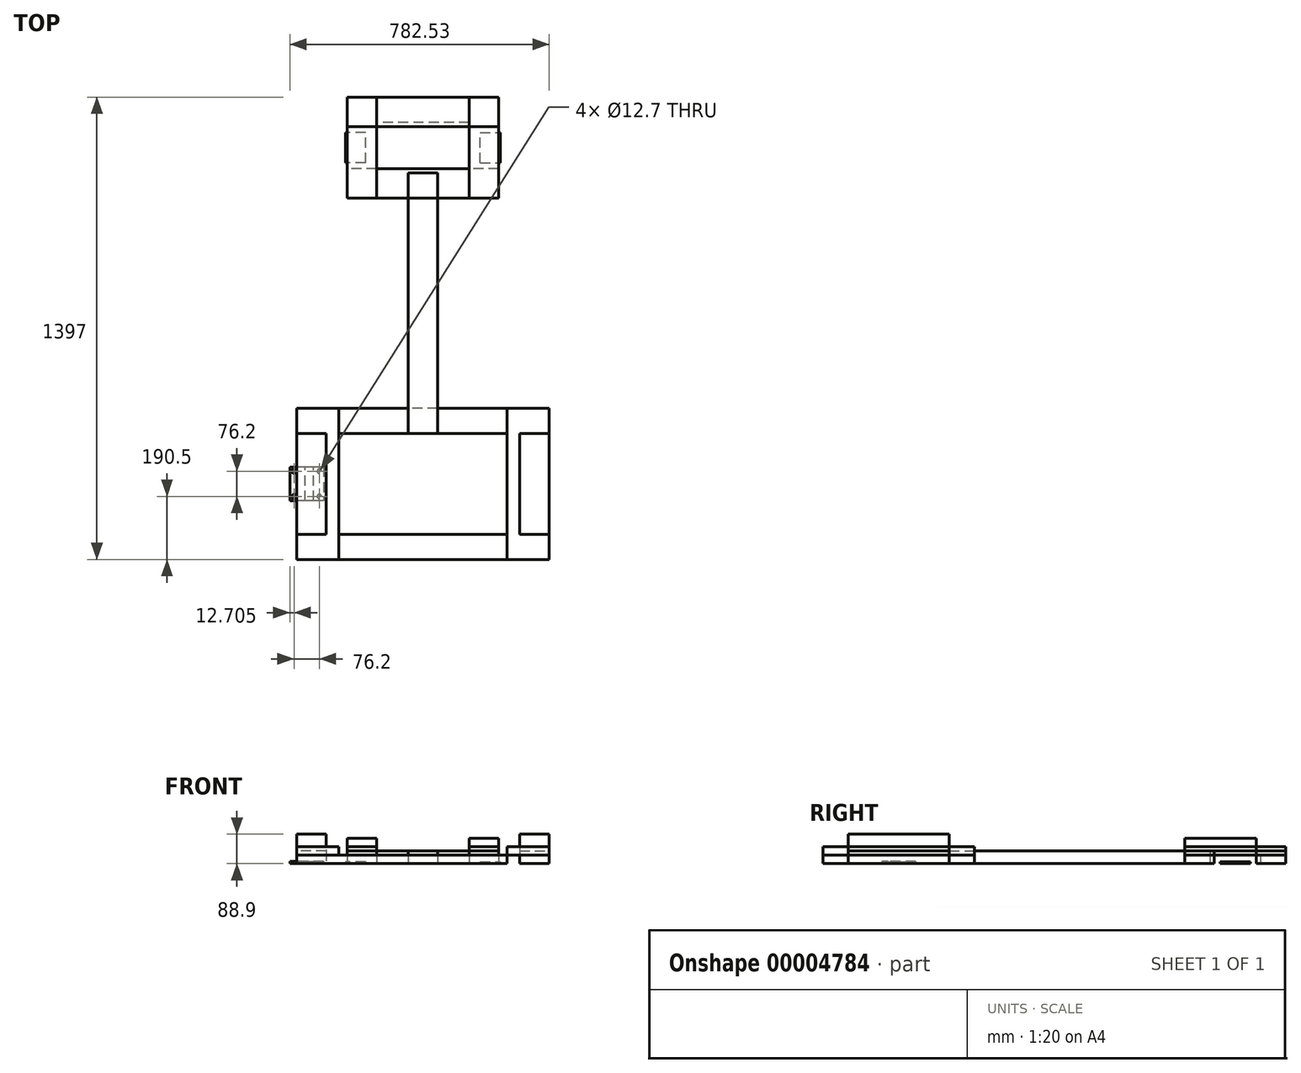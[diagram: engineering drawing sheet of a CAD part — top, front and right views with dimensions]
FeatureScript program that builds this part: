
annotation { "Feature Type Name" : "Feature", "Feature Type Description" : "" }
export const myFeature = defineFeature(function(context is Context, id is Id, definition is map)
    precondition{}
    {
        {
            var Q0;
            Q0=qCreatedBy(makeId("Top.planeOp"),FACE);
            var sketch = newSketch(context, id + "F0", { "sketchPlane" : qUnion([Q0])});
            skLineSegment(sketch, "E0.bottom", {"start": v(44.45, 152.4) * mm, "end": v(-44.45, 152.4) * mm});
            skLineSegment(sketch, "E0.top", {"start": v(44.45, 939.8) * mm, "end": v(-44.45, 939.8) * mm});
            skLineSegment(sketch, "E0.left", {"start": v(44.45, 152.4) * mm, "end": v(44.45, 939.8) * mm});
            skLineSegment(sketch, "E0.right", {"start": v(-44.45, 152.4) * mm, "end": v(-44.45, 939.8) * mm});
            skPoint(sketch, "E0.middle", {"position": v(0, 546.1) * mm});
            skLineSegment(sketch, "E1.bottom", {"start": v(-254, -228.6) * mm, "end": v(-381, -228.6) * mm});
            skLineSegment(sketch, "E1.top", {"start": v(-254, 228.6) * mm, "end": v(-381, 228.6) * mm});
            skLineSegment(sketch, "E1.left", {"start": v(-254, -228.6) * mm, "end": v(-254, 228.6) * mm});
            skLineSegment(sketch, "E1.right", {"start": v(-381, -228.6) * mm, "end": v(-381, 228.6) * mm});
            skPoint(sketch, "E1.middle", {"position": v(-317.5, 0) * mm});
            skLineSegment(sketch, "E2.MirrorCS", {"start": v(254, 228.6) * mm, "end": v(381, 228.6) * mm});
            skLineSegment(sketch, "E3.MirrorCS", {"start": v(381, -228.6) * mm, "end": v(381, 228.6) * mm});
            skLineSegment(sketch, "E4.MirrorCS", {"start": v(254, -228.6) * mm, "end": v(254, 228.6) * mm});
            skLineSegment(sketch, "E5.MirrorCS", {"start": v(254, -228.6) * mm, "end": v(381, -228.6) * mm});
            skLineSegment(sketch, "E6.bottom", {"start": v(381, 152.4) * mm, "end": v(-381, 152.4) * mm});
            skLineSegment(sketch, "E6.top", {"start": v(381, 228.6) * mm, "end": v(-381, 228.6) * mm});
            skLineSegment(sketch, "E6.left", {"start": v(381, 152.4) * mm, "end": v(381, 228.6) * mm});
            skLineSegment(sketch, "E6.right", {"start": v(-381, 152.4) * mm, "end": v(-381, 228.6) * mm});
            skPoint(sketch, "E6.middle", {"position": v(0, 190.5) * mm});
            skPoint(sketch, "E7.MirrorP", {"position": v(0, -190.5) * mm});
            skLineSegment(sketch, "E8.MirrorCS", {"start": v(381, -228.6) * mm, "end": v(-381, -228.6) * mm});
            skLineSegment(sketch, "E9.MirrorCS", {"start": v(381, -152.4) * mm, "end": v(381, -228.6) * mm});
            skLineSegment(sketch, "E10.MirrorCS", {"start": v(-381, 228.6) * mm, "end": v(-381, -228.6) * mm});
            skLineSegment(sketch, "E11.MirrorCS", {"start": v(381, -152.4) * mm, "end": v(-381, -152.4) * mm});
            skLineSegment(sketch, "E12.bottom", {"start": v(-139.7, 863.6) * mm, "end": v(-228.6, 863.6) * mm});
            skLineSegment(sketch, "E12.top", {"start": v(-139.7, 1168.4) * mm, "end": v(-228.6, 1168.4) * mm});
            skLineSegment(sketch, "E12.left", {"start": v(-139.7, 863.6) * mm, "end": v(-139.7, 1168.4) * mm});
            skLineSegment(sketch, "E12.right", {"start": v(-228.6, 863.6) * mm, "end": v(-228.6, 1168.4) * mm});
            skPoint(sketch, "E12.middle", {"position": v(-184.15, 1016) * mm});
            skLineSegment(sketch, "E13", {"start": v(0, 0) * mm, "end": v(0, 2577.34) * mm, "construction": true});
            skLineSegment(sketch, "E14.MirrorCS", {"start": v(139.7, 863.6) * mm, "end": v(139.7, 1168.4) * mm});
            skLineSegment(sketch, "E15.MirrorCS", {"start": v(139.7, 863.6) * mm, "end": v(228.6, 863.6) * mm});
            skLineSegment(sketch, "E16.MirrorCS", {"start": v(228.6, 863.6) * mm, "end": v(228.6, 1168.4) * mm});
            skLineSegment(sketch, "E17.MirrorCS", {"start": v(139.7, 1168.4) * mm, "end": v(228.6, 1168.4) * mm});
            skLineSegment(sketch, "E18", {"start": v(-560.55, 1016) * mm, "end": v(837.57, 1016) * mm, "construction": true});
            skPoint(sketch, "E18.startSnap0", {"position": v(-228.6, 1016) * mm});
            skPoint(sketch, "E18.endSnap0", {"position": v(-228.6, 1016) * mm});
            skLineSegment(sketch, "E19.bottom", {"start": v(228.6, 1092.2) * mm, "end": v(-228.6, 1092.2) * mm});
            skLineSegment(sketch, "E19.top", {"start": v(228.6, 1168.4) * mm, "end": v(-228.6, 1168.4) * mm});
            skLineSegment(sketch, "E19.left", {"start": v(228.6, 1092.2) * mm, "end": v(228.6, 1168.4) * mm});
            skLineSegment(sketch, "E19.right", {"start": v(-228.6, 1092.2) * mm, "end": v(-228.6, 1168.4) * mm});
            skPoint(sketch, "E19.middle", {"position": v(0, 1130.3) * mm});
            skLineSegment(sketch, "E20.MirrorCS", {"start": v(228.6, 939.8) * mm, "end": v(-228.6, 939.8) * mm});
            skLineSegment(sketch, "E21.MirrorCS", {"start": v(-228.6, 939.8) * mm, "end": v(-228.6, 863.6) * mm});
            skLineSegment(sketch, "E22.MirrorCS", {"start": v(228.6, 863.6) * mm, "end": v(-228.6, 863.6) * mm});
            skLineSegment(sketch, "E23.MirrorCS", {"start": v(228.6, 939.8) * mm, "end": v(228.6, 863.6) * mm});
            skSolve(sketch);
        }
        {
            var Q0;
            Q0=qCreatedBy(makeId("Top.planeOp"),FACE);
            var sketch = newSketch(context, id + "F1", { "sketchPlane" : qUnion([Q0])});
            skLineSegment(sketch, "E24.bottom", {"start": v(-292.1, -152.4) * mm, "end": v(-381, -152.4) * mm});
            skLineSegment(sketch, "E24.top", {"start": v(-292.1, 152.4) * mm, "end": v(-381, 152.4) * mm});
            skLineSegment(sketch, "E24.left", {"start": v(-292.1, -152.4) * mm, "end": v(-292.1, 152.4) * mm});
            skLineSegment(sketch, "E24.right", {"start": v(-381, -152.4) * mm, "end": v(-381, 152.4) * mm});
            skPoint(sketch, "E24.middle", {"position": v(-336.55, 0) * mm});
            skLineSegment(sketch, "E25.MirrorCS", {"start": v(292.1, 152.4) * mm, "end": v(381, 152.4) * mm});
            skLineSegment(sketch, "E26.MirrorCS", {"start": v(292.1, -152.4) * mm, "end": v(292.1, 152.4) * mm});
            skLineSegment(sketch, "E27.MirrorCS", {"start": v(381, -152.4) * mm, "end": v(381, 152.4) * mm});
            skLineSegment(sketch, "E28.MirrorCS", {"start": v(292.1, -152.4) * mm, "end": v(381, -152.4) * mm});
            skLineSegment(sketch, "E29.bottom", {"start": v(228.6, 1168.4) * mm, "end": v(-228.6, 1168.4) * mm});
            skLineSegment(sketch, "E29.top", {"start": v(228.6, 1079.5) * mm, "end": v(-228.6, 1079.5) * mm});
            skLineSegment(sketch, "E29.left", {"start": v(228.6, 1168.4) * mm, "end": v(228.6, 1079.5) * mm});
            skLineSegment(sketch, "E29.right", {"start": v(-228.6, 1168.4) * mm, "end": v(-228.6, 1079.5) * mm});
            skPoint(sketch, "E29.middle", {"position": v(0, 1123.95) * mm});
            skLineSegment(sketch, "E30.MirrorCS", {"start": v(228.6, 952.5) * mm, "end": v(-228.6, 952.5) * mm});
            skLineSegment(sketch, "E31.MirrorCS", {"start": v(228.6, 863.6) * mm, "end": v(-228.6, 863.6) * mm});
            skLineSegment(sketch, "E32.MirrorCS", {"start": v(228.6, 863.6) * mm, "end": v(228.6, 952.5) * mm});
            skLineSegment(sketch, "E33.MirrorCS", {"start": v(-228.6, 863.6) * mm, "end": v(-228.6, 952.5) * mm});
            skLineSegment(sketch, "E34.bottom", {"start": v(-139.7, 863.6) * mm, "end": v(-228.6, 863.6) * mm});
            skLineSegment(sketch, "E34.top", {"start": v(-139.7, 1168.4) * mm, "end": v(-228.6, 1168.4) * mm});
            skLineSegment(sketch, "E34.left", {"start": v(-139.7, 863.6) * mm, "end": v(-139.7, 1168.4) * mm});
            skLineSegment(sketch, "E34.right", {"start": v(-228.6, 863.6) * mm, "end": v(-228.6, 1168.4) * mm});
            skPoint(sketch, "E34.middle", {"position": v(-184.15, 1016) * mm});
            skLineSegment(sketch, "E35.MirrorCS", {"start": v(139.7, 1168.4) * mm, "end": v(228.6, 1168.4) * mm});
            skLineSegment(sketch, "E36.MirrorCS", {"start": v(228.6, 863.6) * mm, "end": v(228.6, 1168.4) * mm});
            skLineSegment(sketch, "E37.MirrorCS", {"start": v(139.7, 863.6) * mm, "end": v(139.7, 1168.4) * mm});
            skLineSegment(sketch, "E38.MirrorCS", {"start": v(-228.6, 863.6) * mm, "end": v(228.6, 863.6) * mm});
            skLineSegment(sketch, "E39.bottom", {"start": v(-323.85, -228.6) * mm, "end": v(-349.25, -228.6) * mm});
            skLineSegment(sketch, "E39.top", {"start": v(-323.85, 228.6) * mm, "end": v(-349.25, 228.6) * mm});
            skLineSegment(sketch, "E39.left", {"start": v(-323.85, -228.6) * mm, "end": v(-323.85, 228.6) * mm});
            skLineSegment(sketch, "E39.right", {"start": v(-349.25, -228.6) * mm, "end": v(-349.25, 228.6) * mm});
            skSolve(sketch);
        }
        {
            var Q0;
            Q0=makeQuery(id+"F1.imprint","IMPRINT",FACE,{"disambiguationData":[TD([[makeQuery(id+"F1.imprint","IMPRINT",EDGE,{"derivedFrom":sQuery(id+"F1.wireOp",EDGE,"E24.bottom")}),-1.0]])]});
            var Q1;
            Q1=makeQuery(id+"F1.imprint","IMPRINT",FACE,{"disambiguationData":[TD([[makeQuery(id+"F1.imprint","IMPRINT",EDGE,{"derivedFrom":sQuery(id+"F1.wireOp",EDGE,"E25.MirrorCS")}),-1.0]])]});
            extrude(context, id + "F2", {"entities" : qUnion([Q0, Q1]), "depth" : 88.9 * mm, "offsetDistance" : 25.4 * mm});
        }
        {
            var Q0;
            Q0=makeQuery(id+"F1.imprint","IMPRINT",FACE,{"disambiguationData":[TD([[makeQuery(id+"F1.imprint","IMPRINT",EDGE,{"derivedFrom":sQuery(id+"F1.wireOp",EDGE,"E24.bottom")}),-1.0]])]});
            var Q1;
            Q1=makeQuery(id+"F1.imprint","IMPRINT",FACE,{"disambiguationData":[TD([[makeQuery(id+"F1.imprint","IMPRINT",EDGE,{"derivedFrom":sQuery(id+"F1.wireOp",EDGE,"E25.MirrorCS")}),-1.0]])]});
            extrude(context, id + "F3", {"entities" : qUnion([Q0, Q1]), "depth" : 38.1 * mm, "offsetDistance" : 25.4 * mm});
        }
        {
            var Q0;
            {var subQ0=sQuery(id+"F1.wireOp",EDGE,"E37.MirrorCS");var subQ1=sQuery(id+"F1.wireOp",EDGE,"E30.MirrorCS");var subQ2=makeQuery(id+"F1.imprint","INTERSECT",VERTEX,{"derivedFrom":[subQ1,subQ0]});Q0=makeQuery(id+"F1.imprint","IMPRINT",FACE,{"disambiguationData":[TD([[makeQuery(id+"F1.imprint","IMPRINT",EDGE,{"disambiguationData":[TD([[subQ2,-1.0]])],"derivedFrom":subQ1}),1.0]])]});}
            var Q1;
            {var subQ0=sQuery(id+"F1.wireOp",EDGE,"E36.MirrorCS");var subQ1=sQuery(id+"F1.wireOp",EDGE,"E30.MirrorCS");var subQ2=makeQuery(id+"F1.imprint","INTERSECT",VERTEX,{"derivedFrom":[subQ1,subQ0]});Q1=makeQuery(id+"F1.imprint","IMPRINT",FACE,{"disambiguationData":[TD([[makeQuery(id+"F1.imprint","IMPRINT",EDGE,{"disambiguationData":[TD([[subQ2,-1.0]])],"derivedFrom":subQ1}),1.0]])]});}
            var Q2;
            {var subQ0=sQuery(id+"F1.wireOp",EDGE,"E34.right");var subQ1=sQuery(id+"F1.wireOp",EDGE,"E30.MirrorCS");var subQ2=makeQuery(id+"F1.imprint","INTERSECT",VERTEX,{"derivedFrom":[subQ1,subQ0]});Q2=makeQuery(id+"F1.imprint","IMPRINT",FACE,{"disambiguationData":[TD([[makeQuery(id+"F1.imprint","IMPRINT",EDGE,{"disambiguationData":[TD([[subQ2,1.0]])],"derivedFrom":subQ1}),1.0]])]});}
            var Q3;
            {var subQ5=sQuery(id+"F1.wireOp",EDGE,"E34.top");Q3=makeQuery(id+"F1.imprint","IMPRINT",FACE,{"disambiguationData":[TD([[makeQuery(id+"F1.imprint","IMPRINT",EDGE,{"derivedFrom":subQ5}),1.0]])]});}
            var Q4;
            {var subQ0=sQuery(id+"F1.wireOp",EDGE,"E29.bottom");Q4=makeQuery(id+"F1.imprint","IMPRINT",FACE,{"disambiguationData":[TD([[makeQuery(id+"F1.imprint","IMPRINT",EDGE,{"derivedFrom":subQ0}),1.0]])]});}
            var Q5;
            {var subQ5=sQuery(id+"F1.wireOp",EDGE,"E35.MirrorCS");Q5=makeQuery(id+"F1.imprint","IMPRINT",FACE,{"disambiguationData":[TD([[makeQuery(id+"F1.imprint","IMPRINT",EDGE,{"derivedFrom":subQ5}),-1.0]])]});}
            extrude(context, id + "F4", {"entities" : qUnion([Q0, Q1, Q2, Q3, Q4, Q5]), "depth" : 38.1 * mm, "offsetDistance" : 25.4 * mm});
        }
        {
            var Q0;
            {var subQ5=sQuery(id+"F1.wireOp",EDGE,"E34.top");Q0=makeQuery(id+"F1.imprint","IMPRINT",FACE,{"disambiguationData":[TD([[makeQuery(id+"F1.imprint","IMPRINT",EDGE,{"derivedFrom":subQ5}),1.0]])]});}
            var Q1;
            {var subQ0=sQuery(id+"F1.wireOp",EDGE,"E34.right");var subQ1=sQuery(id+"F1.wireOp",EDGE,"E29.top");var subQ2=makeQuery(id+"F1.imprint","INTERSECT",VERTEX,{"derivedFrom":[subQ1,subQ0]});Q1=makeQuery(id+"F1.imprint","IMPRINT",FACE,{"disambiguationData":[TD([[makeQuery(id+"F1.imprint","IMPRINT",EDGE,{"disambiguationData":[TD([[subQ2,1.0]])],"derivedFrom":subQ1}),1.0]])]});}
            var Q2;
            {var subQ0=sQuery(id+"F1.wireOp",EDGE,"E34.right");var subQ1=sQuery(id+"F1.wireOp",EDGE,"E30.MirrorCS");var subQ2=makeQuery(id+"F1.imprint","INTERSECT",VERTEX,{"derivedFrom":[subQ1,subQ0]});Q2=makeQuery(id+"F1.imprint","IMPRINT",FACE,{"disambiguationData":[TD([[makeQuery(id+"F1.imprint","IMPRINT",EDGE,{"disambiguationData":[TD([[subQ2,1.0]])],"derivedFrom":subQ1}),1.0]])]});}
            var Q3;
            {var subQ0=sQuery(id+"F1.wireOp",EDGE,"E36.MirrorCS");var subQ1=sQuery(id+"F1.wireOp",EDGE,"E30.MirrorCS");var subQ2=makeQuery(id+"F1.imprint","INTERSECT",VERTEX,{"derivedFrom":[subQ1,subQ0]});Q3=makeQuery(id+"F1.imprint","IMPRINT",FACE,{"disambiguationData":[TD([[makeQuery(id+"F1.imprint","IMPRINT",EDGE,{"disambiguationData":[TD([[subQ2,-1.0]])],"derivedFrom":subQ1}),1.0]])]});}
            var Q4;
            {var subQ0=sQuery(id+"F1.wireOp",EDGE,"E36.MirrorCS");var subQ1=sQuery(id+"F1.wireOp",EDGE,"E29.top");var subQ2=makeQuery(id+"F1.imprint","INTERSECT",VERTEX,{"derivedFrom":[subQ1,subQ0]});Q4=makeQuery(id+"F1.imprint","IMPRINT",FACE,{"disambiguationData":[TD([[makeQuery(id+"F1.imprint","IMPRINT",EDGE,{"disambiguationData":[TD([[subQ2,-1.0]])],"derivedFrom":subQ1}),1.0]])]});}
            var Q5;
            {var subQ5=sQuery(id+"F1.wireOp",EDGE,"E35.MirrorCS");Q5=makeQuery(id+"F1.imprint","IMPRINT",FACE,{"disambiguationData":[TD([[makeQuery(id+"F1.imprint","IMPRINT",EDGE,{"derivedFrom":subQ5}),-1.0]])]});}
            extrude(context, id + "F5", {"entities" : qUnion([Q0, Q1, Q2, Q3, Q4, Q5]), "depth" : 38.1 * mm, "offsetDistance" : 25.4 * mm});
        }
        {
            var Q0;
            Q0=makeQuery(id+"F5.opExtrude","SWEPT_BODY",BODY,{"disambiguationData":[OSD([sQuery(id+"F1.wireOp",EDGE,"E34.top"),sQuery(id+"F1.wireOp",EDGE,"E34.left"),sQuery(id+"F1.wireOp",EDGE,"E34.right"),sQuery(id+"F1.wireOp",EDGE,"E38.MirrorCS")])]});
            var Q1;
            Q1=makeQuery(id+"F5.opExtrude","SWEPT_BODY",BODY,{"disambiguationData":[OSD([sQuery(id+"F1.wireOp",EDGE,"E35.MirrorCS"),sQuery(id+"F1.wireOp",EDGE,"E36.MirrorCS"),sQuery(id+"F1.wireOp",EDGE,"E37.MirrorCS"),sQuery(id+"F1.wireOp",EDGE,"E38.MirrorCS")])]});
            transform(context, id + "F6", {"entities" : qUnion([Q0, Q1]), "transformType" : TransformType.TRANSLATION_3D, "dx" : 0 * mm, "dy" : 0 * mm, "dz" : 38.1 * mm, "makeCopy" : false});
        }
        {
            var Q0;
            {var subQ0=sQuery(id+"F0.wireOp",EDGE,"E6.top");var subQ1=sQuery(id+"F0.wireOp",EDGE,"E1.left");var subQ2=makeQuery(id+"F0.imprint","INTERSECT",VERTEX,{"derivedFrom":[subQ1,subQ0]});Q0=makeQuery(id+"F0.imprint","IMPRINT",FACE,{"disambiguationData":[TD([[makeQuery(id+"F0.imprint","IMPRINT",EDGE,{"disambiguationData":[TD([[subQ2,1.0]])],"derivedFrom":subQ1}),1.0]])]});}
            var Q1;
            {var subQ0=sQuery(id+"F0.wireOp",EDGE,"E6.bottom");var subQ1=sQuery(id+"F0.wireOp",EDGE,"E0.right");var subQ2=makeQuery(id+"F0.imprint","INTERSECT",VERTEX,{"derivedFrom":[subQ1,subQ0]});Q1=makeQuery(id+"F0.imprint","IMPRINT",FACE,{"disambiguationData":[TD([[makeQuery(id+"F0.imprint","IMPRINT",EDGE,{"disambiguationData":[TD([[subQ2,-1.0]])],"derivedFrom":subQ1}),1.0]])]});}
            var Q2;
            {var subQ0=sQuery(id+"F0.wireOp",EDGE,"E6.bottom");var subQ1=sQuery(id+"F0.wireOp",EDGE,"E0.left");var subQ2=makeQuery(id+"F0.imprint","INTERSECT",VERTEX,{"derivedFrom":[subQ1,subQ0]});Q2=makeQuery(id+"F0.imprint","IMPRINT",FACE,{"disambiguationData":[TD([[makeQuery(id+"F0.imprint","IMPRINT",EDGE,{"disambiguationData":[TD([[subQ2,-1.0]])],"derivedFrom":subQ1}),-1.0]])]});}
            var Q3;
            {var subQ0=sQuery(id+"F0.wireOp",EDGE,"E6.bottom");var subQ1=sQuery(id+"F0.wireOp",EDGE,"E0.left");var subQ2=makeQuery(id+"F0.imprint","INTERSECT",VERTEX,{"derivedFrom":[subQ1,subQ0]});Q3=makeQuery(id+"F0.imprint","IMPRINT",FACE,{"disambiguationData":[TD([[makeQuery(id+"F0.imprint","IMPRINT",EDGE,{"disambiguationData":[TD([[subQ2,-1.0]])],"derivedFrom":subQ1}),1.0]])]});}
            var Q4;
            {var subQ5=sQuery(id+"F0.wireOp",EDGE,"E6.left");Q4=makeQuery(id+"F0.imprint","IMPRINT",FACE,{"disambiguationData":[TD([[makeQuery(id+"F0.imprint","IMPRINT",EDGE,{"derivedFrom":subQ5}),1.0]])]});}
            var Q5;
            {var subQ0=sQuery(id+"F0.wireOp",EDGE,"E8.MirrorCS");var subQ1=sQuery(id+"F0.wireOp",EDGE,"E1.left");var subQ2=makeQuery(id+"F0.imprint","INTERSECT",VERTEX,{"derivedFrom":[subQ1,subQ0]});Q5=makeQuery(id+"F0.imprint","IMPRINT",FACE,{"disambiguationData":[TD([[makeQuery(id+"F0.imprint","IMPRINT",EDGE,{"disambiguationData":[TD([[subQ2,-1.0]])],"derivedFrom":subQ1}),1.0]])]});}
            var Q6;
            {var subQ0=sQuery(id+"F0.wireOp",EDGE,"E8.MirrorCS");var subQ1=sQuery(id+"F0.wireOp",EDGE,"E1.left");var subQ2=makeQuery(id+"F0.imprint","INTERSECT",VERTEX,{"derivedFrom":[subQ1,subQ0]});Q6=makeQuery(id+"F0.imprint","IMPRINT",FACE,{"disambiguationData":[TD([[makeQuery(id+"F0.imprint","IMPRINT",EDGE,{"disambiguationData":[TD([[subQ2,-1.0]])],"derivedFrom":subQ1}),-1.0]])]});}
            var Q7;
            {var subQ5=sQuery(id+"F0.wireOp",EDGE,"E9.MirrorCS");Q7=makeQuery(id+"F0.imprint","IMPRINT",FACE,{"disambiguationData":[TD([[makeQuery(id+"F0.imprint","IMPRINT",EDGE,{"derivedFrom":subQ5}),-1.0]])]});}
            extrude(context, id + "F7", {"entities" : qUnion([Q0, Q1, Q2, Q3, Q4, Q5, Q6, Q7]), "depth" : 25.4 * mm, "offsetDistance" : 25.4 * mm});
        }
        {
            var Q0;
            {var subQ0=sQuery(id+"F0.wireOp",EDGE,"E6.top");var subQ1=sQuery(id+"F0.wireOp",EDGE,"E1.left");var subQ2=makeQuery(id+"F0.imprint","INTERSECT",VERTEX,{"derivedFrom":[subQ1,subQ0]});Q0=makeQuery(id+"F0.imprint","IMPRINT",FACE,{"disambiguationData":[TD([[makeQuery(id+"F0.imprint","IMPRINT",EDGE,{"disambiguationData":[TD([[subQ2,1.0]])],"derivedFrom":subQ1}),1.0]])]});}
            var Q1;
            {var subQ0=sQuery(id+"F0.wireOp",EDGE,"E11.MirrorCS");var subQ1=sQuery(id+"F0.wireOp",EDGE,"E1.left");var subQ2=makeQuery(id+"F0.imprint","INTERSECT",VERTEX,{"derivedFrom":[subQ1,subQ0]});Q1=makeQuery(id+"F0.imprint","IMPRINT",FACE,{"disambiguationData":[TD([[makeQuery(id+"F0.imprint","IMPRINT",EDGE,{"disambiguationData":[TD([[subQ2,-1.0]])],"derivedFrom":subQ1}),1.0]])]});}
            var Q2;
            {var subQ0=sQuery(id+"F0.wireOp",EDGE,"E8.MirrorCS");var subQ1=sQuery(id+"F0.wireOp",EDGE,"E1.left");var subQ2=makeQuery(id+"F0.imprint","INTERSECT",VERTEX,{"derivedFrom":[subQ1,subQ0]});Q2=makeQuery(id+"F0.imprint","IMPRINT",FACE,{"disambiguationData":[TD([[makeQuery(id+"F0.imprint","IMPRINT",EDGE,{"disambiguationData":[TD([[subQ2,-1.0]])],"derivedFrom":subQ1}),1.0]])]});}
            var Q3;
            {var subQ5=sQuery(id+"F0.wireOp",EDGE,"E9.MirrorCS");Q3=makeQuery(id+"F0.imprint","IMPRINT",FACE,{"disambiguationData":[TD([[makeQuery(id+"F0.imprint","IMPRINT",EDGE,{"derivedFrom":subQ5}),-1.0]])]});}
            var Q4;
            {var subQ5=sQuery(id+"F0.wireOp",EDGE,"E6.left");Q4=makeQuery(id+"F0.imprint","IMPRINT",FACE,{"disambiguationData":[TD([[makeQuery(id+"F0.imprint","IMPRINT",EDGE,{"derivedFrom":subQ5}),1.0]])]});}
            var Q5;
            {var subQ0=sQuery(id+"F0.wireOp",EDGE,"E3.MirrorCS");Q5=makeQuery(id+"F0.imprint","IMPRINT",FACE,{"disambiguationData":[TD([[makeQuery(id+"F0.imprint","IMPRINT",EDGE,{"derivedFrom":subQ0}),1.0]])]});}
            extrude(context, id + "F8", {"entities" : qUnion([Q0, Q1, Q2, Q3, Q4, Q5]), "depth" : 25.4 * mm, "offsetDistance" : 25.4 * mm});
        }
        {
            var Q0;
            {var subQ5=sQuery(id+"F0.wireOp",EDGE,"E19.right");Q0=makeQuery(id+"F0.imprint","IMPRINT",FACE,{"disambiguationData":[TD([[makeQuery(id+"F0.imprint","IMPRINT",EDGE,{"derivedFrom":subQ5}),-1.0]])]});}
            var Q1;
            {var subQ0=sQuery(id+"F0.wireOp",EDGE,"E19.top");var subQ1=sQuery(id+"F0.wireOp",EDGE,"E12.left");var subQ2=makeQuery(id+"F0.imprint","INTERSECT",VERTEX,{"derivedFrom":[subQ1,subQ0]});Q1=makeQuery(id+"F0.imprint","IMPRINT",FACE,{"disambiguationData":[TD([[makeQuery(id+"F0.imprint","IMPRINT",EDGE,{"disambiguationData":[TD([[subQ2,1.0]])],"derivedFrom":subQ1}),-1.0]])]});}
            var Q2;
            {var subQ5=sQuery(id+"F0.wireOp",EDGE,"E19.left");Q2=makeQuery(id+"F0.imprint","IMPRINT",FACE,{"disambiguationData":[TD([[makeQuery(id+"F0.imprint","IMPRINT",EDGE,{"derivedFrom":subQ5}),1.0]])]});}
            var Q3;
            {var subQ5=sQuery(id+"F0.wireOp",EDGE,"E23.MirrorCS");Q3=makeQuery(id+"F0.imprint","IMPRINT",FACE,{"disambiguationData":[TD([[makeQuery(id+"F0.imprint","IMPRINT",EDGE,{"derivedFrom":subQ5}),-1.0]])]});}
            var Q4;
            {var subQ0=sQuery(id+"F0.wireOp",EDGE,"E20.MirrorCS");var subQ1=sQuery(id+"F0.wireOp",EDGE,"E0.left");var subQ2=makeQuery(id+"F0.imprint","INTERSECT",VERTEX,{"derivedFrom":[subQ1,subQ0]});Q4=makeQuery(id+"F0.imprint","IMPRINT",FACE,{"disambiguationData":[TD([[makeQuery(id+"F0.imprint","IMPRINT",EDGE,{"disambiguationData":[TD([[subQ2,1.0]])],"derivedFrom":subQ1}),-1.0]])]});}
            var Q5;
            {var subQ0=sQuery(id+"F0.wireOp",EDGE,"E20.MirrorCS");var subQ1=sQuery(id+"F0.wireOp",EDGE,"E0.left");var subQ2=makeQuery(id+"F0.imprint","INTERSECT",VERTEX,{"derivedFrom":[subQ1,subQ0]});Q5=makeQuery(id+"F0.imprint","IMPRINT",FACE,{"disambiguationData":[TD([[makeQuery(id+"F0.imprint","IMPRINT",EDGE,{"disambiguationData":[TD([[subQ2,1.0]])],"derivedFrom":subQ1}),1.0]])]});}
            var Q6;
            {var subQ0=sQuery(id+"F0.wireOp",EDGE,"E20.MirrorCS");var subQ1=sQuery(id+"F0.wireOp",EDGE,"E0.right");var subQ2=makeQuery(id+"F0.imprint","INTERSECT",VERTEX,{"derivedFrom":[subQ1,subQ0]});Q6=makeQuery(id+"F0.imprint","IMPRINT",FACE,{"disambiguationData":[TD([[makeQuery(id+"F0.imprint","IMPRINT",EDGE,{"disambiguationData":[TD([[subQ2,1.0]])],"derivedFrom":subQ1}),1.0]])]});}
            var Q7;
            {var subQ5=sQuery(id+"F0.wireOp",EDGE,"E21.MirrorCS");Q7=makeQuery(id+"F0.imprint","IMPRINT",FACE,{"disambiguationData":[TD([[makeQuery(id+"F0.imprint","IMPRINT",EDGE,{"derivedFrom":subQ5}),1.0]])]});}
            extrude(context, id + "F9", {"entities" : qUnion([Q0, Q1, Q2, Q3, Q4, Q5, Q6, Q7]), "depth" : 25.4 * mm, "offsetDistance" : 25.4 * mm});
        }
        {
            var Q0;
            {var subQ5=sQuery(id+"F0.wireOp",EDGE,"E19.right");Q0=makeQuery(id+"F0.imprint","IMPRINT",FACE,{"disambiguationData":[TD([[makeQuery(id+"F0.imprint","IMPRINT",EDGE,{"derivedFrom":subQ5}),-1.0]])]});}
            var Q1;
            {var subQ5=sQuery(id+"F0.wireOp",EDGE,"E12.right");Q1=makeQuery(id+"F0.imprint","IMPRINT",FACE,{"disambiguationData":[TD([[makeQuery(id+"F0.imprint","IMPRINT",EDGE,{"derivedFrom":subQ5}),-1.0]])]});}
            var Q2;
            {var subQ5=sQuery(id+"F0.wireOp",EDGE,"E21.MirrorCS");Q2=makeQuery(id+"F0.imprint","IMPRINT",FACE,{"disambiguationData":[TD([[makeQuery(id+"F0.imprint","IMPRINT",EDGE,{"derivedFrom":subQ5}),1.0]])]});}
            var Q3;
            {var subQ5=sQuery(id+"F0.wireOp",EDGE,"E23.MirrorCS");Q3=makeQuery(id+"F0.imprint","IMPRINT",FACE,{"disambiguationData":[TD([[makeQuery(id+"F0.imprint","IMPRINT",EDGE,{"derivedFrom":subQ5}),-1.0]])]});}
            var Q4;
            {var subQ5=sQuery(id+"F0.wireOp",EDGE,"E16.MirrorCS");Q4=makeQuery(id+"F0.imprint","IMPRINT",FACE,{"disambiguationData":[TD([[makeQuery(id+"F0.imprint","IMPRINT",EDGE,{"derivedFrom":subQ5}),1.0]])]});}
            var Q5;
            {var subQ5=sQuery(id+"F0.wireOp",EDGE,"E19.left");Q5=makeQuery(id+"F0.imprint","IMPRINT",FACE,{"disambiguationData":[TD([[makeQuery(id+"F0.imprint","IMPRINT",EDGE,{"derivedFrom":subQ5}),1.0]])]});}
            extrude(context, id + "F10", {"entities" : qUnion([Q0, Q1, Q2, Q3, Q4, Q5]), "depth" : 25.4 * mm, "offsetDistance" : 25.4 * mm});
        }
        {
            var Q0;
            Q0=makeQuery(id+"F10.opExtrude","SWEPT_BODY",BODY,{"disambiguationData":[OSD([sQuery(id+"F0.wireOp",EDGE,"E14.MirrorCS"),sQuery(id+"F0.wireOp",EDGE,"E16.MirrorCS"),sQuery(id+"F0.wireOp",EDGE,"E19.top"),sQuery(id+"F0.wireOp",EDGE,"E19.left"),sQuery(id+"F0.wireOp",EDGE,"E22.MirrorCS"),sQuery(id+"F0.wireOp",EDGE,"E23.MirrorCS")])]});
            var Q1;
            Q1=makeQuery(id+"F10.opExtrude","SWEPT_BODY",BODY,{"disambiguationData":[OSD([sQuery(id+"F0.wireOp",EDGE,"E12.left"),sQuery(id+"F0.wireOp",EDGE,"E12.right"),sQuery(id+"F0.wireOp",EDGE,"E19.top"),sQuery(id+"F0.wireOp",EDGE,"E19.right"),sQuery(id+"F0.wireOp",EDGE,"E21.MirrorCS"),sQuery(id+"F0.wireOp",EDGE,"E22.MirrorCS")])]});
            transform(context, id + "F11", {"entities" : qUnion([Q0, Q1]), "transformType" : TransformType.TRANSLATION_3D, "dx" : 0 * mm, "dy" : 0 * mm, "dz" : 25.4 * mm, "makeCopy" : false});
        }
        {
            var Q0;
            Q0=makeQuery(id+"F8.opExtrude","SWEPT_BODY",BODY,{"disambiguationData":[OSD([sQuery(id+"F0.wireOp",EDGE,"E1.left"),sQuery(id+"F0.wireOp",EDGE,"E6.top"),sQuery(id+"F0.wireOp",EDGE,"E8.MirrorCS"),sQuery(id+"F0.wireOp",EDGE,"E1.right")])]});
            var Q1;
            Q1=makeQuery(id+"F8.opExtrude","SWEPT_BODY",BODY,{"disambiguationData":[OSD([sQuery(id+"F0.wireOp",EDGE,"E3.MirrorCS"),sQuery(id+"F0.wireOp",EDGE,"E4.MirrorCS"),sQuery(id+"F0.wireOp",EDGE,"E6.top"),sQuery(id+"F0.wireOp",EDGE,"E6.left"),sQuery(id+"F0.wireOp",EDGE,"E8.MirrorCS"),sQuery(id+"F0.wireOp",EDGE,"E9.MirrorCS")])]});
            transform(context, id + "F12", {"entities" : qUnion([Q0, Q1]), "transformType" : TransformType.TRANSLATION_3D, "dx" : 0 * mm, "dy" : 0 * mm, "dz" : 25.4 * mm, "makeCopy" : false});
        }
        {
            var Q0;
            {var subQ0=sQuery(id+"F0.wireOp",EDGE,"E6.top");var subQ1=sQuery(id+"F0.wireOp",EDGE,"E0.left");var subQ2=makeQuery(id+"F0.imprint","INTERSECT",VERTEX,{"derivedFrom":[subQ1,subQ0]});Q0=makeQuery(id+"F0.imprint","IMPRINT",FACE,{"disambiguationData":[TD([[makeQuery(id+"F0.imprint","IMPRINT",EDGE,{"disambiguationData":[TD([[subQ2,-1.0]])],"derivedFrom":subQ1}),1.0]])]});}
            var Q1;
            {var subQ0=sQuery(id+"F0.wireOp",EDGE,"E20.MirrorCS");var subQ1=sQuery(id+"F0.wireOp",EDGE,"E0.left");var subQ2=makeQuery(id+"F0.imprint","INTERSECT",VERTEX,{"derivedFrom":[subQ1,subQ0]});Q1=makeQuery(id+"F0.imprint","IMPRINT",FACE,{"disambiguationData":[TD([[makeQuery(id+"F0.imprint","IMPRINT",EDGE,{"disambiguationData":[TD([[subQ2,1.0]])],"derivedFrom":subQ1}),1.0]])]});}
            var Q2;
            {var subQ0=sQuery(id+"F0.wireOp",EDGE,"E6.bottom");var subQ1=sQuery(id+"F0.wireOp",EDGE,"E0.left");var subQ2=makeQuery(id+"F0.imprint","INTERSECT",VERTEX,{"derivedFrom":[subQ1,subQ0]});Q2=makeQuery(id+"F0.imprint","IMPRINT",FACE,{"disambiguationData":[TD([[makeQuery(id+"F0.imprint","IMPRINT",EDGE,{"disambiguationData":[TD([[subQ2,-1.0]])],"derivedFrom":subQ1}),1.0]])]});}
            extrude(context, id + "F13", {"entities" : qUnion([Q0, Q1, Q2]), "depth" : 38.1 * mm, "offsetDistance" : 25.4 * mm});
        }
        {
            var Q0;
            Q0=qCreatedBy(makeId("Top.planeOp"),FACE);
            var sketch = newSketch(context, id + "F14", { "sketchPlane" : qUnion([Q0])});
            skLineSegment(sketch, "E40.bottom", {"start": v(-355.6, -203.2) * mm, "end": v(-381, -203.2) * mm});
            skLineSegment(sketch, "E40.top", {"start": v(-355.6, 203.2) * mm, "end": v(-381, 203.2) * mm});
            skLineSegment(sketch, "E40.left", {"start": v(-355.6, -203.2) * mm, "end": v(-355.6, 203.2) * mm});
            skLineSegment(sketch, "E40.right", {"start": v(-381, -203.2) * mm, "end": v(-381, 203.2) * mm});
            skPoint(sketch, "E40.middle", {"position": v(-368.3, 0) * mm});
            skLineSegment(sketch, "E41.bottom", {"start": v(381, 228.6) * mm, "end": v(-381, 228.6) * mm});
            skLineSegment(sketch, "E41.top", {"start": v(381, 203.2) * mm, "end": v(-381, 203.2) * mm});
            skLineSegment(sketch, "E41.left", {"start": v(381, 228.6) * mm, "end": v(381, 203.2) * mm});
            skLineSegment(sketch, "E41.right", {"start": v(-381, 228.6) * mm, "end": v(-381, 203.2) * mm});
            skPoint(sketch, "E41.middle", {"position": v(0, 215.9) * mm});
            skLineSegment(sketch, "E42.MirrorCS", {"start": v(381, -228.6) * mm, "end": v(-381, -228.6) * mm});
            skLineSegment(sketch, "E43.MirrorCS", {"start": v(381, -203.2) * mm, "end": v(-381, -203.2) * mm});
            skLineSegment(sketch, "E44.MirrorCS", {"start": v(381, -228.6) * mm, "end": v(381, -203.2) * mm});
            skLineSegment(sketch, "E45.MirrorCS", {"start": v(-381, -228.6) * mm, "end": v(-381, -203.2) * mm});
            skLineSegment(sketch, "E46.MirrorCS", {"start": v(355.6, 203.2) * mm, "end": v(381, 203.2) * mm});
            skLineSegment(sketch, "E47.MirrorCS", {"start": v(355.6, -203.2) * mm, "end": v(355.6, 203.2) * mm});
            skLineSegment(sketch, "E48.MirrorCS", {"start": v(381, -203.2) * mm, "end": v(381, 203.2) * mm});
            skLineSegment(sketch, "E49.MirrorCS", {"start": v(-381, -203.2) * mm, "end": v(381, -203.2) * mm});
            skLineSegment(sketch, "E50.bottom", {"start": v(-330.2, -50.8) * mm, "end": v(-381, -50.8) * mm});
            skLineSegment(sketch, "E50.top", {"start": v(-330.2, 50.8) * mm, "end": v(-381, 50.8) * mm});
            skLineSegment(sketch, "E50.left", {"start": v(-330.2, -50.8) * mm, "end": v(-330.2, 50.8) * mm});
            skLineSegment(sketch, "E50.right", {"start": v(-381, -50.8) * mm, "end": v(-381, 50.8) * mm});
            skPoint(sketch, "E50.middle", {"position": v(-355.6, 0) * mm});
            skLineSegment(sketch, "E51.bottom", {"start": v(-330.2, -203.2) * mm, "end": v(-355.6, -203.2) * mm});
            skLineSegment(sketch, "E51.top", {"start": v(-330.2, 203.2) * mm, "end": v(-355.6, 203.2) * mm});
            skLineSegment(sketch, "E51.left", {"start": v(-330.2, -203.2) * mm, "end": v(-330.2, 203.2) * mm});
            skPoint(sketch, "E51.middle", {"position": v(-342.9, 0) * mm});
            skLineSegment(sketch, "E52.MirrorCS", {"start": v(-381, 203.2) * mm, "end": v(381, 203.2) * mm});
            skLineSegment(sketch, "E53.MirrorCS", {"start": v(330.2, -203.2) * mm, "end": v(330.2, 203.2) * mm});
            skLineSegment(sketch, "E54.MirrorCS", {"start": v(330.2, -50.8) * mm, "end": v(330.2, 50.8) * mm});
            skLineSegment(sketch, "E55.MirrorCS", {"start": v(330.2, -50.8) * mm, "end": v(381, -50.8) * mm});
            skLineSegment(sketch, "E56.MirrorCS", {"start": v(381, -50.8) * mm, "end": v(381, 50.8) * mm});
            skLineSegment(sketch, "E57.MirrorCS", {"start": v(330.2, 50.8) * mm, "end": v(381, 50.8) * mm});
            skLineSegment(sketch, "E58.bottom", {"start": v(228.6, 1143) * mm, "end": v(-228.6, 1143) * mm});
            skLineSegment(sketch, "E58.top", {"start": v(228.6, 1168.4) * mm, "end": v(-228.6, 1168.4) * mm});
            skLineSegment(sketch, "E58.left", {"start": v(228.6, 1143) * mm, "end": v(228.6, 1168.4) * mm});
            skLineSegment(sketch, "E58.right", {"start": v(-228.6, 1143) * mm, "end": v(-228.6, 1168.4) * mm});
            skPoint(sketch, "E58.middle", {"position": v(0, 1155.7) * mm});
            skLineSegment(sketch, "E59.0", {"start": v(0, 0) * mm, "end": v(0, 2577.34) * mm, "construction": true});
            skLineSegment(sketch, "E59.1", {"start": v(-560.55, 1016) * mm, "end": v(837.57, 1016) * mm, "construction": true});
            skLineSegment(sketch, "E60.MirrorCS", {"start": v(228.6, 863.6) * mm, "end": v(-228.6, 863.6) * mm});
            skLineSegment(sketch, "E61.MirrorCS", {"start": v(228.6, 889) * mm, "end": v(-228.6, 889) * mm});
            skLineSegment(sketch, "E62.MirrorCS", {"start": v(-228.6, 889) * mm, "end": v(-228.6, 863.6) * mm});
            skLineSegment(sketch, "E63.MirrorCS", {"start": v(228.6, 889) * mm, "end": v(228.6, 863.6) * mm});
            skLineSegment(sketch, "E64.bottom", {"start": v(-203.2, 889) * mm, "end": v(-228.6, 889) * mm});
            skLineSegment(sketch, "E64.top", {"start": v(-203.2, 1143) * mm, "end": v(-228.6, 1143) * mm});
            skLineSegment(sketch, "E64.left", {"start": v(-203.2, 889) * mm, "end": v(-203.2, 1143) * mm});
            skLineSegment(sketch, "E64.right", {"start": v(-228.6, 889) * mm, "end": v(-228.6, 1143) * mm});
            skPoint(sketch, "E64.middle", {"position": v(-215.9, 1016) * mm});
            skLineSegment(sketch, "E65.MirrorCS", {"start": v(-228.6, 1143) * mm, "end": v(228.6, 1143) * mm});
            skLineSegment(sketch, "E66.MirrorCS", {"start": v(203.2, 889) * mm, "end": v(203.2, 1143) * mm});
            skLineSegment(sketch, "E67.MirrorCS", {"start": v(-228.6, 889) * mm, "end": v(228.6, 889) * mm});
            skLineSegment(sketch, "E68.MirrorCS", {"start": v(228.6, 889) * mm, "end": v(228.6, 1143) * mm});
            skLineSegment(sketch, "E69.bottom", {"start": v(-177.8, 889) * mm, "end": v(-203.2, 889) * mm});
            skLineSegment(sketch, "E69.top", {"start": v(-177.8, 1143) * mm, "end": v(-203.2, 1143) * mm});
            skLineSegment(sketch, "E69.left", {"start": v(-177.8, 889) * mm, "end": v(-177.8, 1143) * mm});
            skPoint(sketch, "E69.middle", {"position": v(-190.5, 1016) * mm});
            skLineSegment(sketch, "E70.MirrorCS", {"start": v(177.8, 889) * mm, "end": v(177.8, 1143) * mm});
            skLineSegment(sketch, "E71.MirrorCS", {"start": v(177.8, 1143) * mm, "end": v(203.2, 1143) * mm});
            skLineSegment(sketch, "E72.MirrorCS", {"start": v(177.8, 889) * mm, "end": v(203.2, 889) * mm});
            skLineSegment(sketch, "E73.bottom", {"start": v(-173.04, 969.96) * mm, "end": v(-233.36, 969.96) * mm});
            skLineSegment(sketch, "E73.top", {"start": v(-173.04, 1062.04) * mm, "end": v(-233.36, 1062.04) * mm});
            skLineSegment(sketch, "E73.left", {"start": v(-173.04, 969.96) * mm, "end": v(-173.04, 1062.04) * mm});
            skLineSegment(sketch, "E73.right", {"start": v(-233.36, 969.96) * mm, "end": v(-233.36, 1062.04) * mm});
            skPoint(sketch, "E73.middle", {"position": v(-203.2, 1016) * mm});
            skLineSegment(sketch, "E74.MirrorCS", {"start": v(173.04, 969.96) * mm, "end": v(173.04, 1062.04) * mm});
            skLineSegment(sketch, "E75.MirrorCS", {"start": v(173.04, 1062.04) * mm, "end": v(233.36, 1062.04) * mm});
            skLineSegment(sketch, "E76.MirrorCS", {"start": v(173.04, 969.96) * mm, "end": v(233.36, 969.96) * mm});
            skLineSegment(sketch, "E77.MirrorCS", {"start": v(233.36, 969.96) * mm, "end": v(233.36, 1062.04) * mm});
            skSolve(sketch);
        }
        {
            var Q0;
            {var subQ5=sQuery(id+"F14.wireOp",EDGE,"E50.right");Q0=makeQuery(id+"F14.imprint","IMPRINT",FACE,{"disambiguationData":[TD([[makeQuery(id+"F14.imprint","IMPRINT",EDGE,{"derivedFrom":subQ5}),-1.0]])]});}
            var Q1;
            {var subQ0=sQuery(id+"F14.wireOp",EDGE,"E51.left");var subQ1=sQuery(id+"F14.wireOp",EDGE,"E50.bottom");var subQ2=makeQuery(id+"F14.imprint","INTERSECT",VERTEX,{"derivedFrom":[subQ1,subQ0]});Q1=makeQuery(id+"F14.imprint","IMPRINT",FACE,{"disambiguationData":[TD([[makeQuery(id+"F14.imprint","IMPRINT",EDGE,{"disambiguationData":[TD([[subQ2,-1.0]])],"derivedFrom":subQ1}),-1.0]])]});}
            var Q2;
            {var subQ0=sQuery(id+"F14.wireOp",EDGE,"E50.left");Q2=makeQuery(id+"F14.imprint","IMPRINT",FACE,{"disambiguationData":[TD([[makeQuery(id+"F14.imprint","IMPRINT",EDGE,{"derivedFrom":subQ0}),1.0]])]});}
            var Q3;
            {var subQ5=sQuery(id+"F14.wireOp",EDGE,"E56.MirrorCS");Q3=makeQuery(id+"F14.imprint","IMPRINT",FACE,{"disambiguationData":[TD([[makeQuery(id+"F14.imprint","IMPRINT",EDGE,{"derivedFrom":subQ5}),1.0]])]});}
            var Q4;
            {var subQ5=sQuery(id+"F14.wireOp",EDGE,"E54.MirrorCS");Q4=makeQuery(id+"F14.imprint","IMPRINT",FACE,{"disambiguationData":[TD([[makeQuery(id+"F14.imprint","IMPRINT",EDGE,{"derivedFrom":subQ5}),-1.0]])]});}
            var Q5;
            {var subQ5=sQuery(id+"F14.wireOp",EDGE,"E77.MirrorCS");Q5=makeQuery(id+"F14.imprint","IMPRINT",FACE,{"disambiguationData":[TD([[makeQuery(id+"F14.imprint","IMPRINT",EDGE,{"derivedFrom":subQ5}),1.0]])]});}
            var Q6;
            {var subQ0=sQuery(id+"F14.wireOp",EDGE,"E76.MirrorCS");var subQ1=sQuery(id+"F14.wireOp",EDGE,"E68.MirrorCS");var subQ2=makeQuery(id+"F14.imprint","INTERSECT",VERTEX,{"derivedFrom":[subQ1,subQ0]});Q6=makeQuery(id+"F14.imprint","IMPRINT",FACE,{"disambiguationData":[TD([[makeQuery(id+"F14.imprint","IMPRINT",EDGE,{"disambiguationData":[TD([[subQ2,-1.0]])],"derivedFrom":subQ1}),1.0]])]});}
            var Q7;
            {var subQ0=sQuery(id+"F14.wireOp",EDGE,"E76.MirrorCS");var subQ1=sQuery(id+"F14.wireOp",EDGE,"E70.MirrorCS");var subQ2=makeQuery(id+"F14.imprint","INTERSECT",VERTEX,{"derivedFrom":[subQ1,subQ0]});Q7=makeQuery(id+"F14.imprint","IMPRINT",FACE,{"disambiguationData":[TD([[makeQuery(id+"F14.imprint","IMPRINT",EDGE,{"disambiguationData":[TD([[subQ2,-1.0]])],"derivedFrom":subQ1}),-1.0]])]});}
            var Q8;
            {var subQ5=sQuery(id+"F14.wireOp",EDGE,"E74.MirrorCS");Q8=makeQuery(id+"F14.imprint","IMPRINT",FACE,{"disambiguationData":[TD([[makeQuery(id+"F14.imprint","IMPRINT",EDGE,{"derivedFrom":subQ5}),-1.0]])]});}
            var Q9;
            {var subQ5=sQuery(id+"F14.wireOp",EDGE,"E73.left");Q9=makeQuery(id+"F14.imprint","IMPRINT",FACE,{"disambiguationData":[TD([[makeQuery(id+"F14.imprint","IMPRINT",EDGE,{"derivedFrom":subQ5}),1.0]])]});}
            var Q10;
            {var subQ0=sQuery(id+"F14.wireOp",EDGE,"E73.bottom");var subQ1=sQuery(id+"F14.wireOp",EDGE,"E69.left");var subQ2=makeQuery(id+"F14.imprint","INTERSECT",VERTEX,{"derivedFrom":[subQ1,subQ0]});Q10=makeQuery(id+"F14.imprint","IMPRINT",FACE,{"disambiguationData":[TD([[makeQuery(id+"F14.imprint","IMPRINT",EDGE,{"disambiguationData":[TD([[subQ2,-1.0]])],"derivedFrom":subQ1}),1.0]])]});}
            var Q11;
            {var subQ0=sQuery(id+"F14.wireOp",EDGE,"E73.bottom");var subQ1=sQuery(id+"F14.wireOp",EDGE,"E64.right");var subQ2=makeQuery(id+"F14.imprint","INTERSECT",VERTEX,{"derivedFrom":[subQ1,subQ0]});Q11=makeQuery(id+"F14.imprint","IMPRINT",FACE,{"disambiguationData":[TD([[makeQuery(id+"F14.imprint","IMPRINT",EDGE,{"disambiguationData":[TD([[subQ2,-1.0]])],"derivedFrom":subQ1}),-1.0]])]});}
            var Q12;
            {var subQ5=sQuery(id+"F14.wireOp",EDGE,"E73.right");Q12=makeQuery(id+"F14.imprint","IMPRINT",FACE,{"disambiguationData":[TD([[makeQuery(id+"F14.imprint","IMPRINT",EDGE,{"derivedFrom":subQ5}),-1.0]])]});}
            extrude(context, id + "F15", {"entities" : qUnion([Q0, Q1, Q2, Q3, Q4, Q5, Q6, Q7, Q8, Q9, Q10, Q11, Q12]), "depth" : (5 + (5 / 8)) * mm, "offsetDistance" : 25.4 * mm});
        }
        {
            var Q0;
            Q0=qCreatedBy(makeId("Top.planeOp"),FACE);
            var sketch = newSketch(context, id + "F16", { "sketchPlane" : qUnion([Q0])});
            skLineSegment(sketch, "E78.bottom", {"start": v(-299.93, 50.8) * mm, "end": v(-401.53, 50.8) * mm});
            skLineSegment(sketch, "E78.top", {"start": v(-299.93, -50.8) * mm, "end": v(-401.53, -50.8) * mm});
            skLineSegment(sketch, "E78.left", {"start": v(-299.93, 50.8) * mm, "end": v(-299.93, -50.8) * mm});
            skLineSegment(sketch, "E78.right", {"start": v(-401.53, 50.8) * mm, "end": v(-401.53, -50.8) * mm});
            skPoint(sketch, "E78.middle", {"position": v(-350.73, 0) * mm});
            skLineSegment(sketch, "E79.left", {"start": v(-299.93, -50.8) * mm, "end": v(-299.93, 50.8) * mm});
            skLineSegment(sketch, "E79.right", {"start": v(-401.53, -50.8) * mm, "end": v(-401.53, 50.8) * mm});
            skCircle(sketch, "E80", {"center": v(-388.83, -38.1) * mm, "radius": 6.35 * mm});
            skLineSegment(sketch, "E81", {"start": v(-401.53, 0) * mm, "end": v(-299.93, 0) * mm, "construction": true});
            skCircle(sketch, "E82.MirrorC", {"center": v(-388.83, 38.1) * mm, "radius": 6.35 * mm});
            skLineSegment(sketch, "E83", {"start": v(-350.73, 50.8) * mm, "end": v(-350.73, -50.8) * mm, "construction": true});
            skCircle(sketch, "E84.MirrorC", {"center": v(-312.63, 38.1) * mm, "radius": 6.35 * mm});
            skCircle(sketch, "E85.MirrorC", {"center": v(-312.63, -38.1) * mm, "radius": 6.35 * mm});
            skPoint(sketch, "E86", {"position": v(-350.17, 125.2) * mm});
            skSolve(sketch);
        }
        {
            var Q0;
            Q0=makeQuery(id+"F16.imprint","IMPRINT",FACE,{"disambiguationData":[TD([[makeQuery(id+"F16.imprint","IMPRINT",EDGE,{"derivedFrom":sQuery(id+"F16.wireOp",EDGE,"E78.bottom")}),-1.0]])]});
            var Q1;
            Q1=makeQuery(id+"F16.imprint","IMPRINT",FACE,{"disambiguationData":[TD([[makeQuery(id+"F16.imprint","IMPRINT",EDGE,{"derivedFrom":sQuery(id+"F16.wireOp",EDGE,"E78.bottom")}),1.0]])]});
            var Q2;
            Q2=makeQuery(id+"F16.imprint","IMPRINT",FACE,{"disambiguationData":[TD([[makeQuery(id+"F16.imprint","IMPRINT",EDGE,{"derivedFrom":sQuery(id+"F16.wireOp",EDGE,"E78.top")}),-1.0]])]});
            extrude(context, id + "F17", {"entities" : qUnion([Q0, Q1, Q2]), "depth" : 6.35 * mm, "offsetDistance" : 25.4 * mm});
        }
    });
